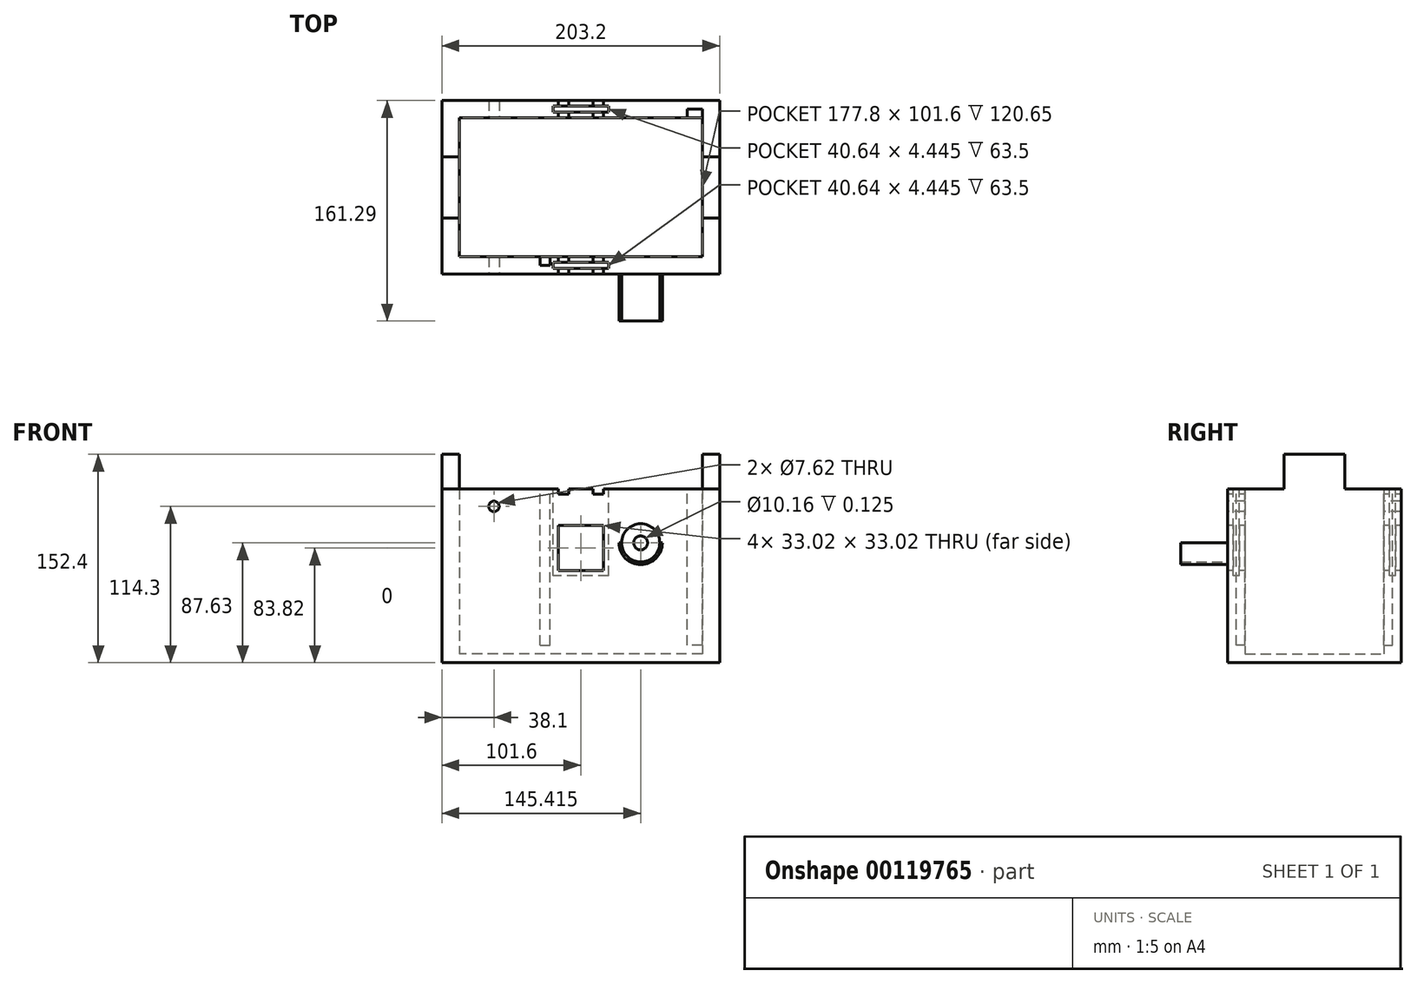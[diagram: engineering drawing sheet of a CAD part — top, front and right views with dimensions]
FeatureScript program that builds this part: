
annotation { "Feature Type Name" : "Feature", "Feature Type Description" : "" }
export const myFeature = defineFeature(function(context is Context, id is Id, definition is map)
    precondition{}
    {
        {
            assignVariable(context, id + "F0", {"name" : "width", "anyValue" : 127 * mm});
        }
        {
            assignVariable(context, id + "F1", {"name" : "wallThickness", "anyValue" : 0.5});
        }
        {
            assignVariable(context, id + "F2", {"name" : "baseThickness", "anyValue" : 6.35 * mm});
        }
        {
            assignVariable(context, id + "F3", {"name" : "height", "anyValue" : 127 * mm});
        }
        {
            assignVariable(context, id + "F4", {"name" : "airMotorHousingLength", "anyValue" : 34.3 * mm});
        }
        {
            assignVariable(context, id + "F5", {"name" : "airMotorLength", "anyValue" : 0.12});
        }
        {
            var Q0;
            Q0=qCreatedBy(makeId("Top.planeOp"),FACE);
            var sketch = newSketch(context, id + "F6", { "sketchPlane" : qUnion([Q0])});
            skLineSegment(sketch, "E0.bottom", {"start": v(0, 0) * mm, "end": v(203.2, 0) * mm});
            skLineSegment(sketch, "E0.top", {"start": v(0, 127) * mm, "end": v(203.2, 127) * mm});
            skLineSegment(sketch, "E0.left", {"start": v(0, 0) * mm, "end": v(0, 127) * mm});
            skLineSegment(sketch, "E0.right", {"start": v(203.2, 0) * mm, "end": v(203.2, 127) * mm});
            skPoint(sketch, "E1", {"position": v(12.7, 12.7) * mm});
            skPoint(sketch, "E2", {"position": v(12.7, 114.3) * mm});
            skPoint(sketch, "E3", {"position": v(190.5, 114.3) * mm});
            skPoint(sketch, "E4", {"position": v(190.5, 12.7) * mm});
            skLineSegment(sketch, "E5", {"start": v(12.7, 12.7) * mm, "end": v(190.5, 12.7) * mm});
            skLineSegment(sketch, "E6", {"start": v(190.5, 114.3) * mm, "end": v(190.5, 12.7) * mm});
            skLineSegment(sketch, "E7", {"start": v(190.5, 114.3) * mm, "end": v(12.7, 114.3) * mm});
            skLineSegment(sketch, "E8", {"start": v(12.7, 12.7) * mm, "end": v(12.7, 114.3) * mm});
            skSolve(sketch);
        }
        {
            var Q0;
            Q0=makeQuery(id+"F6.imprint","IMPRINT",FACE,{"disambiguationData":[TD([[makeQuery(id+"F6.imprint","IMPRINT",EDGE,{"derivedFrom":sQuery(id+"F6.wireOp",EDGE,"E0.bottom")}),1.0]])]});
            extrude(context, id + "F7", {"entities" : qUnion([Q0]), "depth" : getVariable(context, 'height')});
        }
        {
            var Q0;
            Q0=makeQuery(id+"F6.imprint","IMPRINT",FACE,{"disambiguationData":[TD([[makeQuery(id+"F6.imprint","IMPRINT",EDGE,{"derivedFrom":sQuery(id+"F6.wireOp",EDGE,"E5")}),1.0]])]});
            extrude(context, id + "F8", {"entities" : qUnion([Q0]), "operationType" : NewBodyOperationType.ADD, "depth" : getVariable(context, 'baseThickness')});
        }
        {
            var Q0;
            Q0=makeQuery(id+"F7.opExtrude","CAP_FACE",FACE,{"disambiguationData":[OSD([sQuery(id+"F6.wireOp",EDGE,"E0.bottom"),sQuery(id+"F6.wireOp",EDGE,"E0.top"),sQuery(id+"F6.wireOp",EDGE,"E0.left"),sQuery(id+"F6.wireOp",EDGE,"E0.right"),sQuery(id+"F6.wireOp",EDGE,"E5"),sQuery(id+"F6.wireOp",EDGE,"E6"),sQuery(id+"F6.wireOp",EDGE,"E7"),sQuery(id+"F6.wireOp",EDGE,"E8")])],"isStart":false});
            var sketch = newSketch(context, id + "F9", { "sketchPlane" : qUnion([Q0])});
            skPoint(sketch, "E9", {"position": v(101.6, 0) * mm});
            skPoint(sketch, "E10", {"position": v(101.6, 12.7) * mm});
            skLineSegment(sketch, "E11", {"start": v(101.6, 12.7) * mm, "end": v(101.6, 0) * mm});
            skPoint(sketch, "E12", {"position": v(101.6, 6.35) * mm});
            skLineSegment(sketch, "E13.bottom", {"start": v(121.92, 8.57) * mm, "end": v(81.28, 8.57) * mm});
            skLineSegment(sketch, "E13.top", {"start": v(121.92, 4.13) * mm, "end": v(81.28, 4.13) * mm});
            skLineSegment(sketch, "E13.left", {"start": v(121.92, 8.57) * mm, "end": v(121.92, 4.13) * mm});
            skLineSegment(sketch, "E13.right", {"start": v(81.28, 8.57) * mm, "end": v(81.28, 4.13) * mm});
            skPoint(sketch, "E14", {"position": v(101.6, 114.3) * mm});
            skPoint(sketch, "E15", {"position": v(101.6, 127) * mm});
            skLineSegment(sketch, "E16", {"start": v(101.6, 114.3) * mm, "end": v(101.6, 127) * mm});
            skPoint(sketch, "E17", {"position": v(101.6, 120.65) * mm});
            skLineSegment(sketch, "E18.bottom", {"start": v(121.92, 122.87) * mm, "end": v(81.28, 122.87) * mm});
            skLineSegment(sketch, "E18.top", {"start": v(121.92, 118.43) * mm, "end": v(81.28, 118.43) * mm});
            skLineSegment(sketch, "E18.left", {"start": v(121.92, 122.87) * mm, "end": v(121.92, 118.43) * mm});
            skLineSegment(sketch, "E18.right", {"start": v(81.28, 122.87) * mm, "end": v(81.28, 118.43) * mm});
            skSolve(sketch);
        }
        {
            var Q0;
            {var subQ5=sQuery(id+"F9.wireOp",EDGE,"E13.right");Q0=makeQuery(id+"F9.imprint","IMPRINT",FACE,{"disambiguationData":[TD([[makeQuery(id+"F9.imprint","IMPRINT",EDGE,{"derivedFrom":subQ5}),1.0]])]});}
            var Q1;
            {var subQ5=sQuery(id+"F9.wireOp",EDGE,"E13.left");Q1=makeQuery(id+"F9.imprint","IMPRINT",FACE,{"disambiguationData":[TD([[makeQuery(id+"F9.imprint","IMPRINT",EDGE,{"derivedFrom":subQ5}),-1.0]])]});}
            var Q2;
            {var subQ5=sQuery(id+"F9.wireOp",EDGE,"E18.right");Q2=makeQuery(id+"F9.imprint","IMPRINT",FACE,{"disambiguationData":[TD([[makeQuery(id+"F9.imprint","IMPRINT",EDGE,{"derivedFrom":subQ5}),1.0]])]});}
            var Q3;
            {var subQ5=sQuery(id+"F9.wireOp",EDGE,"E18.left");Q3=makeQuery(id+"F9.imprint","IMPRINT",FACE,{"disambiguationData":[TD([[makeQuery(id+"F9.imprint","IMPRINT",EDGE,{"derivedFrom":subQ5}),-1.0]])]});}
            extrude(context, id + "F10", {"entities" : qUnion([Q0, Q1, Q2, Q3]), "operationType" : NewBodyOperationType.REMOVE, "oppositeDirection" : true, "depth" : getVariable(context, 'height') / 2});
        }
        {
            var Q0;
            Q0=makeQuery(id+"F7.opExtrude","SWEPT_FACE",FACE,{"disambiguationData":[OSD([sQuery(id+"F6.wireOp",EDGE,"E0.bottom")])]});
            var sketch = newSketch(context, id + "F11", { "sketchPlane" : qUnion([Q0])});
            skPoint(sketch, "E19", {"position": v(101.6, 127) * mm});
            skPoint(sketch, "E20", {"position": v(121.92, 127) * mm});
            skPoint(sketch, "E21", {"position": v(81.28, 127) * mm});
            skLineSegment(sketch, "E22", {"start": v(81.28, 127) * mm, "end": v(81.28, 63.5) * mm});
            skLineSegment(sketch, "E23", {"start": v(121.92, 127) * mm, "end": v(121.92, 63.5) * mm});
            skLineSegment(sketch, "E24", {"start": v(81.28, 63.5) * mm, "end": v(121.92, 63.5) * mm});
            skCircle(sketch, "E25", {"center": v(145.42, 87.63) * mm, "radius": 13.97 * mm});
            skPoint(sketch, "E26", {"position": v(81.28, 104.14) * mm});
            skPoint(sketch, "E27", {"position": v(121.92, 104.14) * mm});
            skPoint(sketch, "E28", {"position": v(85.1, 67.3) * mm});
            skPoint(sketch, "E29", {"position": v(118.11, 67.3) * mm});
            skLineSegment(sketch, "E30", {"start": v(85.1, 67.3) * mm, "end": v(118.11, 67.3) * mm});
            skLineSegment(sketch, "E31", {"start": v(85.1, 67.3) * mm, "end": v(85.1, 100.33) * mm});
            skLineSegment(sketch, "E32", {"start": v(118.11, 67.3) * mm, "end": v(118.11, 100.33) * mm});
            skLineSegment(sketch, "E33", {"start": v(85.1, 100.33) * mm, "end": v(118.11, 100.33) * mm});
            skCircle(sketch, "E34", {"center": v(145.42, 87.63) * mm, "radius": 5.08 * mm});
            skCircle(sketch, "E35", {"center": v(145.42, 87.63) * mm, "radius": 15.88 * mm});
            skLineSegment(sketch, "E36", {"start": v(145.42, 87.63) * mm, "end": v(161.3, 87.63) * mm});
            skLineSegment(sketch, "E37", {"start": v(145.42, 87.63) * mm, "end": v(129.54, 87.63) * mm});
            skLineSegment(sketch, "E38.bottom", {"start": v(81.28, 127) * mm, "end": v(85.1, 127) * mm});
            skLineSegment(sketch, "E38.top", {"start": v(81.28, 123.2) * mm, "end": v(85.1, 123.2) * mm});
            skLineSegment(sketch, "E38.left", {"start": v(81.28, 127) * mm, "end": v(81.28, 123.2) * mm});
            skLineSegment(sketch, "E38.right", {"start": v(85.1, 127) * mm, "end": v(85.1, 123.2) * mm});
            skLineSegment(sketch, "E39.bottom", {"start": v(121.92, 127) * mm, "end": v(118.11, 127) * mm});
            skLineSegment(sketch, "E39.top", {"start": v(121.92, 123.2) * mm, "end": v(118.11, 123.2) * mm});
            skLineSegment(sketch, "E39.left", {"start": v(121.92, 127) * mm, "end": v(121.92, 123.2) * mm});
            skLineSegment(sketch, "E39.right", {"start": v(118.11, 127) * mm, "end": v(118.11, 123.2) * mm});
            skLineSegment(sketch, "E40.bottom", {"start": v(85.1, 127) * mm, "end": v(92.7, 127) * mm});
            skLineSegment(sketch, "E40.top", {"start": v(85.1, 123.19) * mm, "end": v(92.7, 123.19) * mm});
            skLineSegment(sketch, "E40.left", {"start": v(85.1, 127) * mm, "end": v(85.1, 123.19) * mm});
            skLineSegment(sketch, "E40.right", {"start": v(92.7, 127) * mm, "end": v(92.7, 123.2) * mm});
            skLineSegment(sketch, "E41.bottom", {"start": v(118.11, 127) * mm, "end": v(110.5, 127) * mm});
            skLineSegment(sketch, "E41.top", {"start": v(118.11, 123.2) * mm, "end": v(110.5, 123.2) * mm});
            skLineSegment(sketch, "E41.right", {"start": v(110.5, 127) * mm, "end": v(110.5, 123.2) * mm});
            skSolve(sketch);
        }
        {
            var Q0;
            Q0=makeQuery(id+"F11.imprint","IMPRINT",FACE,{"disambiguationData":[TD([[makeQuery(id+"F11.imprint","IMPRINT",EDGE,{"derivedFrom":sQuery(id+"F11.wireOp",EDGE,"E30")}),1.0]])]});
            var Q1;
            Q1=makeQuery(id+"F11.imprint","IMPRINT",FACE,{"disambiguationData":[TD([[makeQuery(id+"F11.imprint","IMPRINT",EDGE,{"derivedFrom":sQuery(id+"F11.wireOp",EDGE,"E40.bottom")}),-1.0]])]});
            var Q2;
            Q2=makeQuery(id+"F11.imprint","IMPRINT",FACE,{"disambiguationData":[TD([[makeQuery(id+"F11.imprint","IMPRINT",EDGE,{"derivedFrom":sQuery(id+"F11.wireOp",EDGE,"E41.bottom")}),-1.0]])]});
            extrude(context, id + "F12", {"entities" : qUnion([Q0, Q1, Q2]), "operationType" : NewBodyOperationType.REMOVE, "oppositeDirection" : true, "depth" : getVariable(context, 'width')});
        }
        {
            var Q0;
            Q0=makeQuery(id+"F11.imprint","IMPRINT",FACE,{"disambiguationData":[TD([[makeQuery(id+"F11.imprint","IMPRINT",EDGE,{"derivedFrom":sQuery(id+"F11.wireOp",EDGE,"E34")}),1.0]])]});
            extrude(context, id + "F13", {"entities" : qUnion([Q0]), "operationType" : NewBodyOperationType.REMOVE, "oppositeDirection" : true, "depth" : (getVariable(context, 'wallThickness')) * mm});
        }
        {
            var Q0;
            {var subQ0=sQuery(id+"F11.wireOp",EDGE,"E36");var subQ1=sQuery(id+"F11.wireOp",EDGE,"E25");var subQ2=makeQuery(id+"F11.imprint","INTERSECT",VERTEX,{"derivedFrom":[subQ1,subQ0]});Q0=makeQuery(id+"F11.imprint","IMPRINT",FACE,{"disambiguationData":[TD([[makeQuery(id+"F11.imprint","IMPRINT",EDGE,{"disambiguationData":[TD([[subQ2,1.0]])],"derivedFrom":subQ1}),-1.0]])]});}
            var Q1;
            {var subQ0=sQuery(id+"F11.wireOp",EDGE,"E36");var subQ1=sQuery(id+"F11.wireOp",EDGE,"E25");var subQ2=makeQuery(id+"F11.imprint","INTERSECT",VERTEX,{"derivedFrom":[subQ1,subQ0]});Q1=makeQuery(id+"F11.imprint","IMPRINT",FACE,{"disambiguationData":[TD([[makeQuery(id+"F11.imprint","IMPRINT",EDGE,{"disambiguationData":[TD([[subQ2,1.0]])],"derivedFrom":subQ1}),1.0]])]});}
            var Q2;
            {var subQ0=sQuery(id+"F11.wireOp",EDGE,"E36");var subQ1=sQuery(id+"F11.wireOp",EDGE,"E25");var subQ2=makeQuery(id+"F11.imprint","INTERSECT",VERTEX,{"derivedFrom":[subQ1,subQ0]});Q2=makeQuery(id+"F11.imprint","IMPRINT",FACE,{"disambiguationData":[TD([[makeQuery(id+"F11.imprint","IMPRINT",EDGE,{"disambiguationData":[TD([[subQ2,-1.0]])],"derivedFrom":subQ1}),1.0]])]});}
            extrude(context, id + "F14", {"entities" : qUnion([Q0, Q1, Q2]), "operationType" : NewBodyOperationType.REMOVE, "oppositeDirection" : true, "depth" : (getVariable(context, 'wallThickness') - getVariable(context, 'airMotorLength')) * mm});
        }
        {
            var Q0;
            {var subQ0=sQuery(id+"F11.wireOp",EDGE,"E36");var subQ1=sQuery(id+"F11.wireOp",EDGE,"E25");var subQ2=makeQuery(id+"F11.imprint","INTERSECT",VERTEX,{"derivedFrom":[subQ1,subQ0]});Q0=makeQuery(id+"F11.imprint","IMPRINT",FACE,{"disambiguationData":[TD([[makeQuery(id+"F11.imprint","IMPRINT",EDGE,{"disambiguationData":[TD([[subQ2,1.0]])],"derivedFrom":subQ1}),-1.0]])]});}
            extrude(context, id + "F15", {"entities" : qUnion([Q0]), "depth" : getVariable(context, 'airMotorHousingLength')});
        }
        {
            var Q0;
            Q0=makeQuery(id+"F7.opExtrude","CAP_FACE",FACE,{"disambiguationData":[OSD([sQuery(id+"F6.wireOp",EDGE,"E0.bottom"),sQuery(id+"F6.wireOp",EDGE,"E0.top"),sQuery(id+"F6.wireOp",EDGE,"E0.left"),sQuery(id+"F6.wireOp",EDGE,"E0.right"),sQuery(id+"F6.wireOp",EDGE,"E5"),sQuery(id+"F6.wireOp",EDGE,"E6"),sQuery(id+"F6.wireOp",EDGE,"E7"),sQuery(id+"F6.wireOp",EDGE,"E8")])],"isStart":false});
            var sketch = newSketch(context, id + "F16", { "sketchPlane" : qUnion([Q0])});
            skPoint(sketch, "E42", {"position": v(71.97, 12.7) * mm});
            skPoint(sketch, "E43", {"position": v(71.97, 114.3) * mm});
            skLineSegment(sketch, "E44.bottom", {"start": v(190.5, 12.7) * mm, "end": v(179.58, 12.7) * mm});
            skLineSegment(sketch, "E44.top", {"start": v(190.5, 6.35) * mm, "end": v(179.58, 6.35) * mm});
            skLineSegment(sketch, "E44.left", {"start": v(190.5, 12.7) * mm, "end": v(190.5, 6.35) * mm});
            skLineSegment(sketch, "E44.right", {"start": v(179.58, 12.7) * mm, "end": v(179.58, 6.35) * mm});
            skLineSegment(sketch, "E45.bottom", {"start": v(71.97, 12.7) * mm, "end": v(79.08, 12.7) * mm});
            skLineSegment(sketch, "E45.top", {"start": v(71.97, 6.35) * mm, "end": v(79.08, 6.35) * mm});
            skLineSegment(sketch, "E45.left", {"start": v(71.97, 12.7) * mm, "end": v(71.97, 6.35) * mm});
            skLineSegment(sketch, "E45.right", {"start": v(79.08, 12.7) * mm, "end": v(79.08, 6.35) * mm});
            skLineSegment(sketch, "E46.bottom", {"start": v(190.5, 114.3) * mm, "end": v(179.58, 114.3) * mm});
            skLineSegment(sketch, "E46.top", {"start": v(190.5, 120.65) * mm, "end": v(179.58, 120.65) * mm});
            skLineSegment(sketch, "E46.left", {"start": v(190.5, 114.3) * mm, "end": v(190.5, 120.65) * mm});
            skLineSegment(sketch, "E46.right", {"start": v(179.58, 114.3) * mm, "end": v(179.58, 120.65) * mm});
            skLineSegment(sketch, "E47.bottom", {"start": v(71.97, 114.3) * mm, "end": v(79.08, 114.3) * mm});
            skLineSegment(sketch, "E47.top", {"start": v(71.97, 120.65) * mm, "end": v(79.08, 120.65) * mm});
            skLineSegment(sketch, "E47.left", {"start": v(71.97, 114.3) * mm, "end": v(71.97, 120.65) * mm});
            skLineSegment(sketch, "E47.right", {"start": v(79.08, 114.3) * mm, "end": v(79.08, 120.65) * mm});
            skSolve(sketch);
        }
        {
            var Q0;
            Q0=makeQuery(id+"F16.imprint","IMPRINT",FACE,{"disambiguationData":[TD([[makeQuery(id+"F16.imprint","IMPRINT",EDGE,{"derivedFrom":sQuery(id+"F16.wireOp",EDGE,"E44.bottom")}),-1.0]])]});
            var Q1;
            Q1=makeQuery(id+"F16.imprint","IMPRINT",FACE,{"disambiguationData":[TD([[makeQuery(id+"F16.imprint","IMPRINT",EDGE,{"derivedFrom":sQuery(id+"F16.wireOp",EDGE,"E45.bottom")}),-1.0]])]});
            var Q2;
            Q2=makeQuery(id+"F16.imprint","IMPRINT",FACE,{"disambiguationData":[TD([[makeQuery(id+"F16.imprint","IMPRINT",EDGE,{"derivedFrom":sQuery(id+"F16.wireOp",EDGE,"E46.bottom")}),-1.0]])]});
            var Q3;
            Q3=makeQuery(id+"F16.imprint","IMPRINT",FACE,{"disambiguationData":[TD([[makeQuery(id+"F16.imprint","IMPRINT",EDGE,{"derivedFrom":sQuery(id+"F16.wireOp",EDGE,"E47.bottom")}),-1.0]])]});
            extrude(context, id + "F17", {"entities" : qUnion([Q0, Q1, Q2, Q3]), "operationType" : NewBodyOperationType.REMOVE, "oppositeDirection" : true, "depth" : getVariable(context, 'height') - 12.7 * mm});
        }
        {
            var Q0;
            {var subQ0=sQuery(id+"F6.wireOp",EDGE,"E8");var subQ1=sQuery(id+"F6.wireOp",EDGE,"E7");var subQ2=sQuery(id+"F6.wireOp",EDGE,"E0.top");var subQ3=sQuery(id+"F6.wireOp",EDGE,"E6");var subQ4=sQuery(id+"F6.wireOp",EDGE,"E5");var subQ5=sQuery(id+"F6.wireOp",EDGE,"E0.bottom");var subQ6=sQuery(id+"F6.wireOp",EDGE,"E0.left");var subQ7=sQuery(id+"F6.wireOp",EDGE,"E0.right");Q0=makeQuery(id+"F12.boolean.opBoolean","SPLIT",FACE,{"disambiguationData":[TD([makeQuery(id+"F7.opExtrude","SWEPT_FACE",FACE,{"disambiguationData":[OSD([subQ5])]}),makeQuery(id+"F7.opExtrude","SWEPT_FACE",FACE,{"disambiguationData":[OSD([subQ2])]}),makeQuery(id+"F7.opExtrude","SWEPT_FACE",FACE,{"disambiguationData":[OSD([subQ6])]}),makeQuery(id+"F7.opExtrude","SWEPT_FACE",FACE,{"disambiguationData":[OSD([subQ7])]}),makeQuery(id+"F7.opExtrude","SWEPT_FACE",FACE,{"disambiguationData":[OSD([subQ4])]}),makeQuery(id+"F7.opExtrude","SWEPT_FACE",FACE,{"disambiguationData":[OSD([subQ3])]}),makeQuery(id+"F7.opExtrude","SWEPT_FACE",FACE,{"disambiguationData":[OSD([subQ1])]}),makeQuery(id+"F7.opExtrude","SWEPT_FACE",FACE,{"disambiguationData":[OSD([subQ0])]}),makeQuery(id+"F10.boolean.opBoolean","COPY",FACE,{"derivedFrom":makeQuery(id+"F10.opExtrude","SWEPT_FACE",FACE,{"disambiguationData":[OSD([sQuery(id+"F9.wireOp",EDGE,"E13.bottom")])]})}),makeQuery(id+"F10.boolean.opBoolean","COPY",FACE,{"derivedFrom":makeQuery(id+"F10.opExtrude","SWEPT_FACE",FACE,{"disambiguationData":[OSD([sQuery(id+"F9.wireOp",EDGE,"E13.top")])]})}),makeQuery(id+"F10.boolean.opBoolean","COPY",FACE,{"derivedFrom":makeQuery(id+"F10.opExtrude","SWEPT_FACE",FACE,{"disambiguationData":[OSD([sQuery(id+"F9.wireOp",EDGE,"E13.left")])]})}),makeQuery(id+"F10.boolean.opBoolean","COPY",FACE,{"derivedFrom":makeQuery(id+"F10.opExtrude","SWEPT_FACE",FACE,{"disambiguationData":[OSD([sQuery(id+"F9.wireOp",EDGE,"E13.right")])]})}),makeQuery(id+"F12.opExtrude","SWEPT_FACE",FACE,{"disambiguationData":[OSD([sQuery(id+"F11.wireOp",EDGE,"E40.left")])]}),makeQuery(id+"F12.opExtrude","SWEPT_FACE",FACE,{"disambiguationData":[OSD([sQuery(id+"F11.wireOp",EDGE,"E39.right")])]})])],"derivedFrom":makeQuery(id+"F7.opExtrude","CAP_FACE",FACE,{"disambiguationData":[OSD([subQ5,subQ2,subQ6,subQ7,subQ4,subQ3,subQ1,subQ0])],"isStart":false})});}
            var sketch = newSketch(context, id + "F18", { "sketchPlane" : qUnion([Q0])});
            skPoint(sketch, "E48", {"position": v(203.2, 63.5) * mm});
            skPoint(sketch, "E49", {"position": v(0, 63.5) * mm});
            skLineSegment(sketch, "E50.bottom", {"start": v(0, 63.5) * mm, "end": v(12.7, 63.5) * mm});
            skLineSegment(sketch, "E50.top", {"start": v(0, 41.15) * mm, "end": v(12.7, 41.15) * mm});
            skLineSegment(sketch, "E50.left", {"start": v(0, 63.5) * mm, "end": v(0, 41.15) * mm});
            skLineSegment(sketch, "E50.right", {"start": v(12.7, 63.5) * mm, "end": v(12.7, 41.15) * mm});
            skLineSegment(sketch, "E51.top", {"start": v(0, 85.85) * mm, "end": v(12.7, 85.85) * mm});
            skLineSegment(sketch, "E51.left", {"start": v(0, 63.5) * mm, "end": v(0, 85.85) * mm});
            skLineSegment(sketch, "E51.right", {"start": v(12.7, 63.5) * mm, "end": v(12.7, 85.85) * mm});
            skLineSegment(sketch, "E52.bottom", {"start": v(203.2, 63.5) * mm, "end": v(190.5, 63.5) * mm});
            skLineSegment(sketch, "E52.top", {"start": v(203.2, 41.15) * mm, "end": v(190.5, 41.15) * mm});
            skLineSegment(sketch, "E52.left", {"start": v(203.2, 63.5) * mm, "end": v(203.2, 41.15) * mm});
            skLineSegment(sketch, "E52.right", {"start": v(190.5, 63.5) * mm, "end": v(190.5, 41.15) * mm});
            skLineSegment(sketch, "E53.top", {"start": v(203.2, 85.85) * mm, "end": v(190.5, 85.85) * mm});
            skLineSegment(sketch, "E53.left", {"start": v(203.2, 63.5) * mm, "end": v(203.2, 85.85) * mm});
            skLineSegment(sketch, "E53.right", {"start": v(190.5, 63.5) * mm, "end": v(190.5, 85.85) * mm});
            skSolve(sketch);
        }
        {
            var Q0;
            Q0=makeQuery(id+"F18.imprint","IMPRINT",FACE,{"disambiguationData":[TD([[makeQuery(id+"F18.imprint","IMPRINT",EDGE,{"derivedFrom":sQuery(id+"F18.wireOp",EDGE,"E50.top")}),1.0]])]});
            var Q1;
            Q1=makeQuery(id+"F18.imprint","IMPRINT",FACE,{"disambiguationData":[TD([[makeQuery(id+"F18.imprint","IMPRINT",EDGE,{"derivedFrom":sQuery(id+"F18.wireOp",EDGE,"E52.top")}),-1.0]])]});
            var Q2;
            Q2=makeQuery(id+"F18.imprint","IMPRINT",FACE,{"disambiguationData":[TD([[makeQuery(id+"F18.imprint","IMPRINT",EDGE,{"derivedFrom":sQuery(id+"F18.wireOp",EDGE,"E52.bottom")}),-1.0]])]});
            var Q3;
            Q3=makeQuery(id+"F18.imprint","IMPRINT",FACE,{"disambiguationData":[TD([[makeQuery(id+"F18.imprint","IMPRINT",EDGE,{"derivedFrom":sQuery(id+"F18.wireOp",EDGE,"E50.bottom")}),1.0]])]});
            extrude(context, id + "F19", {"entities" : qUnion([Q0, Q1, Q2, Q3]), "operationType" : NewBodyOperationType.ADD, "depth" : 25.4 * mm});
        }
        {
            var Q0;
            Q0=makeQuery(id+"F11.imprint","IMPRINT",FACE,{"disambiguationData":[TD([[makeQuery(id+"F11.imprint","IMPRINT",EDGE,{"derivedFrom":sQuery(id+"F11.wireOp",EDGE,"E22")}),-1.0]])]});
            var sketch = newSketch(context, id + "F20", { "sketchPlane" : qUnion([Q0])});
            skCircle(sketch, "E54", {"center": v(38.1, 114.3) * mm, "radius": 3.81 * mm});
            skSolve(sketch);
        }
        {
            var Q0;
            Q0=makeQuery(id+"F20.imprint","IMPRINT",FACE,{"disambiguationData":[TD([[makeQuery(id+"F20.imprint","IMPRINT",EDGE,{"derivedFrom":sQuery(id+"F20.wireOp",EDGE,"E54")}),1.0]])]});
            extrude(context, id + "F21", {"entities" : qUnion([Q0]), "operationType" : NewBodyOperationType.REMOVE, "oppositeDirection" : true, "depth" : getVariable(context, 'width')});
        }
    });
